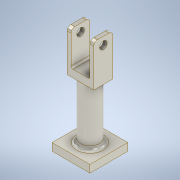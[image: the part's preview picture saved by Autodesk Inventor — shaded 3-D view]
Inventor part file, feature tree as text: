
AUTODESK INVENTOR PART (.ipt)
format: ipt  version: 2022 (Build 260153000, 153)  size: 187,392 bytes
history: native  units: in
note: dims shown in document units (in); Inventor stores cm internally (conversion verified against a paired STEP export)
features: extrude x6, sketch x6, fillet x3
ambient origin geometry x8: Origin, YZ Plane, XZ Plane, XY Plane, X Axis, Y Axis, Z Axis, Center Point
bodies: Solid1 (feature_tree)
feature tree (15):
  extrude  "Extrusion1"  Depth=3.937in
  extrude  "Extrusion2"  Depth=0.7874in TaperAngle=0.0deg
  extrude  "Extrusion3"  Depth=5.9055in TaperAngle=0.0deg
  extrude  "Extrusion4"  Depth=1.378in
  sketch  "Sketch5"  dims[d13=1.378in d14=0.3937in]
  extrude  "Extrusion5"  Depth=0.3937in
  extrude  "Extrusion6"  Depth=3.5433in TaperAngle=0.0deg
  fillet  "Fillet1"  Radius=0.7874in
  fillet  "Fillet2"  Radius=0.7874in
  fillet  "Fillet3"  Radius=0.3937in
  sketch  "Sketch1"  dims[d0=3.937in d1=3.937in]
  sketch  "Sketch2"  dims[d2=3.937in d3=0.7874in d4=0.0in]
  sketch  "Sketch3"  dims[d5=1.9685in d6=5.9055in d7=0.0in]
  sketch  "Sketch4"  dims[d10=0.7874in d11=0.0in d12=1.378in]
  sketch  "Sketch6"  dims[d15=0.3937in d16=3.5433in d17=0.0in d20=0.7874in d23=0.7874in d24=0.3937in d25=0.0in d26=0.3937in d27=0.0in d28=0.1969in d29=0.3937in d30=0.3937in]
